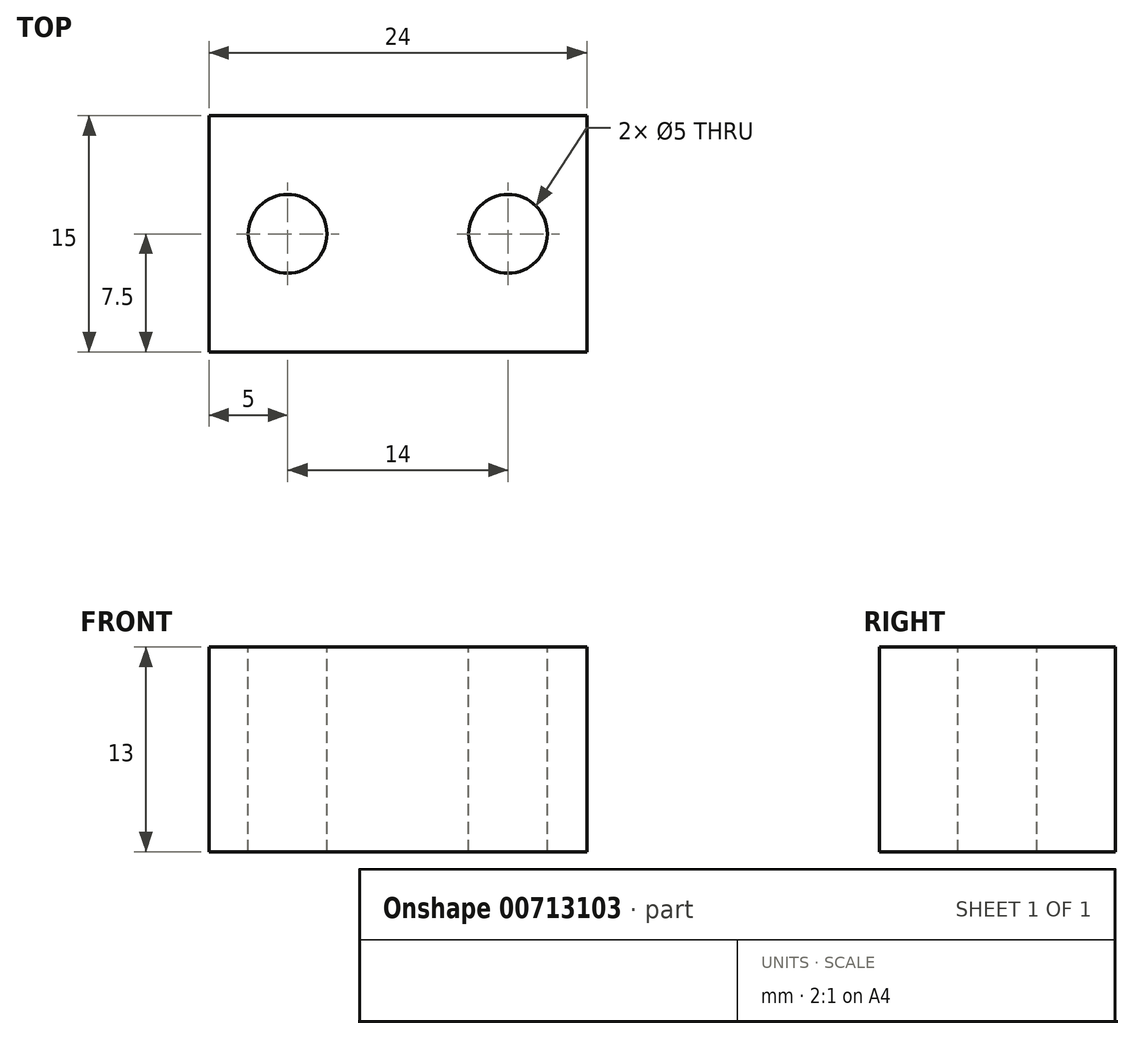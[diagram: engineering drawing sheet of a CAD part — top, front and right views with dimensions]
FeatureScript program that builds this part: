
annotation { "Feature Type Name" : "Feature", "Feature Type Description" : "" }
export const myFeature = defineFeature(function(context is Context, id is Id, definition is map)
    precondition{}
    {
        {
            var Q0;
            Q0=qCreatedBy(makeId("Top.planeOp"),FACE);
            var sketch = newSketch(context, id + "F0", { "sketchPlane" : qUnion([Q0])});
            skLineSegment(sketch, "E0.bottom", {"start": v(12, -7.5) * mm, "end": v(-12, -7.5) * mm});
            skLineSegment(sketch, "E0.top", {"start": v(12, 7.5) * mm, "end": v(-12, 7.5) * mm});
            skLineSegment(sketch, "E0.left", {"start": v(12, -7.5) * mm, "end": v(12, 7.5) * mm});
            skLineSegment(sketch, "E0.right", {"start": v(-12, -7.5) * mm, "end": v(-12, 7.5) * mm});
            skPoint(sketch, "E0.middle", {"position": v(0, 0) * mm});
            skSolve(sketch);
        }
        {
            var Q0;
            Q0=makeQuery(id+"F0.imprint","IMPRINT",FACE,{"disambiguationData":[TD([[makeQuery(id+"F0.imprint","IMPRINT",EDGE,{"derivedFrom":sQuery(id+"F0.wireOp",EDGE,"E0.bottom")}),-1.0]])]});
            extrude(context, id + "F1", {"entities" : qUnion([Q0]), "depth" : 13 * mm, "offsetDistance" : 25 * mm});
        }
        {
            var Q0;
            Q0=makeQuery(id+"F1.opExtrude","CAP_FACE",FACE,{"disambiguationData":[OSD([sQuery(id+"F0.wireOp",EDGE,"E0.bottom"),sQuery(id+"F0.wireOp",EDGE,"E0.top"),sQuery(id+"F0.wireOp",EDGE,"E0.left"),sQuery(id+"F0.wireOp",EDGE,"E0.right")])],"isStart":false});
            var sketch = newSketch(context, id + "F2", { "sketchPlane" : qUnion([Q0])});
            skLineSegment(sketch, "E1", {"start": v(0, 0) * mm, "end": v(7, 0) * mm});
            skLineSegment(sketch, "E2", {"start": v(7, 0) * mm, "end": v(7, 0) * mm});
            skLineSegment(sketch, "E3", {"start": v(0, 0) * mm, "end": v(-7, 0) * mm});
            skSolve(sketch);
        }
        {
            var Q0;
            Q0=sQuery(id+"F2.wireOp",VERTEX,"E3.end");
            var Q1;
            Q1=sQuery(id+"F2.wireOp",VERTEX,"E1.end");
            var Q2;
            Q2=makeQuery(id+"F1.opExtrude","SWEPT_BODY",BODY,{"disambiguationData":[OSD([sQuery(id+"F0.wireOp",EDGE,"E0.bottom"),sQuery(id+"F0.wireOp",EDGE,"E0.top"),sQuery(id+"F0.wireOp",EDGE,"E0.left"),sQuery(id+"F0.wireOp",EDGE,"E0.right")])]});
            hole(context, id + "F3", {"style" : HoleStyle.SIMPLE, "endStyle" : HoleEndStyle.THROUGH, "holeDiameter" : 5 * mm, "majorDiameter" : 5 * mm, "isTappedThrough" : true, "tappedDepth" : 12 * mm, "tapClearance" : 3, "locations" : qUnion([Q0, Q1]), "scope" : qUnion([Q2])});
        }
    });
